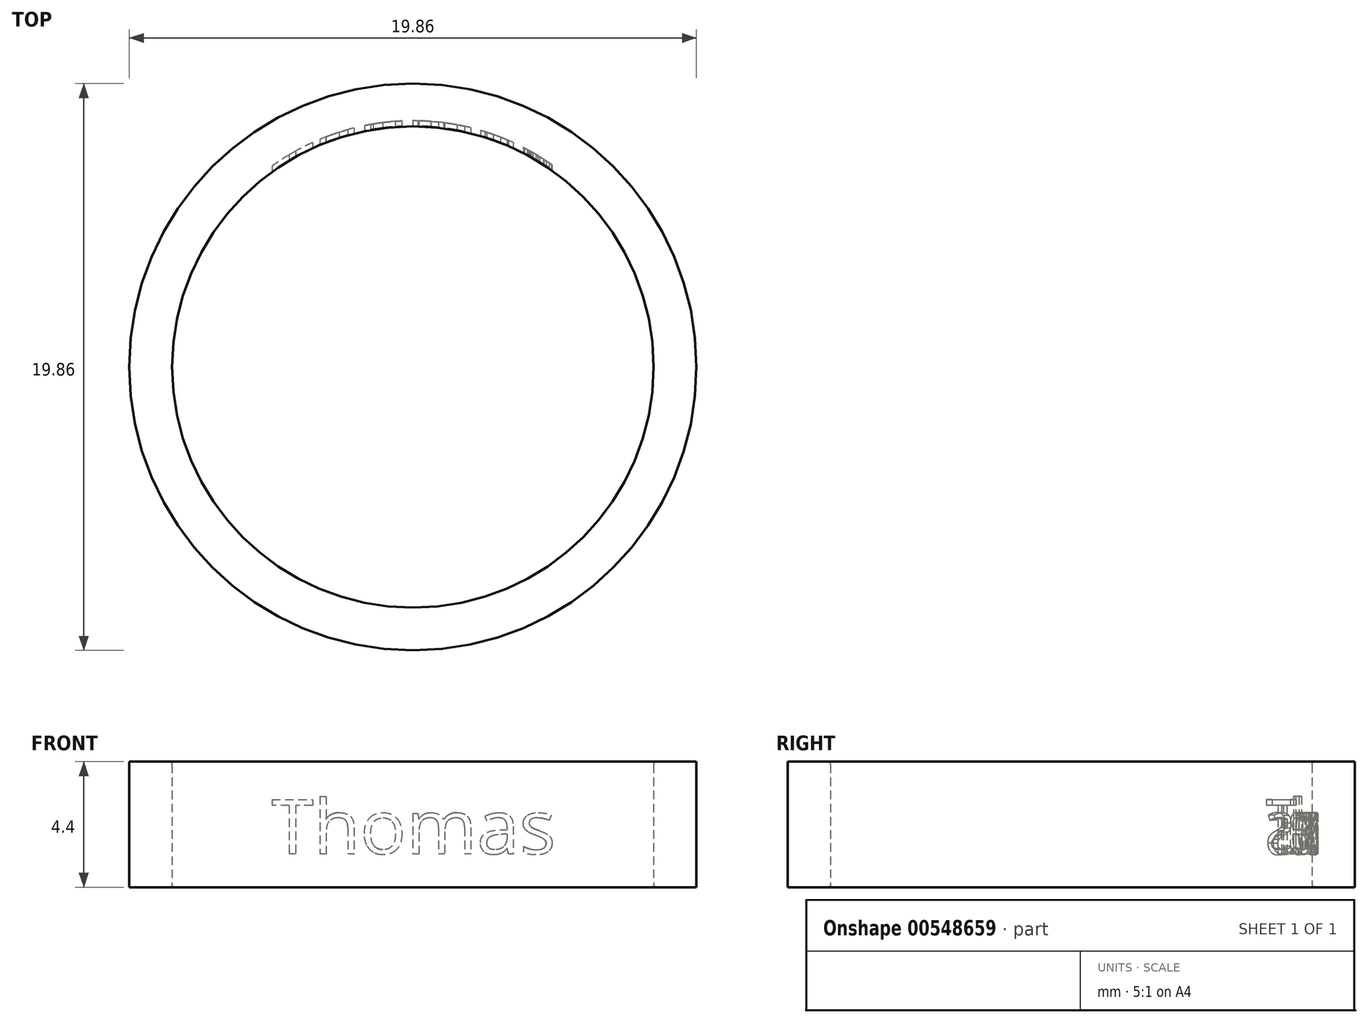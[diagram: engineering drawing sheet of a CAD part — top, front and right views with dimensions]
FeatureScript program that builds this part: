
annotation { "Feature Type Name" : "Feature", "Feature Type Description" : "" }
export const myFeature = defineFeature(function(context is Context, id is Id, definition is map)
    precondition{}
    {
        {
            var Q0;
            Q0=qCreatedBy(makeId("Top.planeOp"),FACE);
            var sketch = newSketch(context, id + "F0", { "sketchPlane" : qUnion([Q0])});
            skCircle(sketch, "E0", {"center": v(0, 0) * mm, "radius": 9.93 * mm});
            skCircle(sketch, "E1.0", {"center": v(0, 0) * mm, "radius": 8.43 * mm});
            skCircle(sketch, "E2.0", {"center": v(0, 0) * mm, "radius": 8.63 * mm, "construction": true});
            skSolve(sketch);
        }
        {
            var Q0;
            Q0=makeQuery(id+"F0.imprint","IMPRINT",FACE,{"disambiguationData":[TD([[makeQuery(id+"F0.imprint","IMPRINT",EDGE,{"derivedFrom":sQuery(id+"F0.wireOp",EDGE,"E0")}),1.0]])]});
            extrude(context, id + "F1", {"entities" : qUnion([Q0]), "depth" : 4.4 * mm, "offsetDistance" : 25 * mm});
        }
        {
            var Q0;
            Q0=qCreatedBy(makeId("Front.planeOp"),FACE);
            var sketch = newSketch(context, id + "F2", { "sketchPlane" : qUnion([Q0])});
            skText(sketch, "E3", { "text": "Thomas\n", "fontName": "OpenSans-Regular.ttf"});
            const initialGuessF2  = {"E3": [-0.00496, 0.00116, 1, 0, 0.00192]};
            skSetInitialGuess(sketch, initialGuessF2);
            skSolve(sketch);
        }
        {
            var Q0;
            Q0=qSketchRegion(id+"F2",true);
            var Q1;
            Q1=qConstructionFilter(qBodyType(qCreatedBy(id+"F2",EDGE),BodyType.WIRE),ConstructionObject.NO);
            var Q2;
            Q2=makeQuery(id+"F1.opExtrude","SWEPT_FACE",FACE,{"disambiguationData":[OSD([sQuery(id+"F0.wireOp",EDGE,"E1.0")])]});
            extrude(context, id + "F3", {"entities" : qUnion([Q0]), "operationType" : NewBodyOperationType.REMOVE, "surfaceEntities" : qUnion([Q1]), "endBound" : BoundingType.UP_TO_SURFACE, "oppositeDirection" : true, "depth" : 25 * mm, "endBoundEntityFace" : qUnion([Q2]), "hasOffset" : true, "offsetDistance" : 0.2 * mm, "offsetOppositeDirection" : true});
        }
        {
            var Q0;
            Q0=qSketchRegion(id+"F2",true);
            var Q1;
            Q1=makeQuery(id+"F1.opExtrude","SWEPT_FACE",FACE,{"disambiguationData":[OSD([sQuery(id+"F0.wireOp",EDGE,"E1.0")])]});
            extrude(context, id + "F4", {"entities" : qUnion([Q0]), "operationType" : NewBodyOperationType.REMOVE, "endBound" : BoundingType.UP_TO_SURFACE, "oppositeDirection" : true, "depth" : 25 * mm, "endBoundEntityFace" : qUnion([Q1]), "offsetDistance" : 25 * mm});
        }
        {
            var Q0;
            Q0=makeQuery(id+"F1.opExtrude","CAP_EDGE",EDGE,{"disambiguationData":[OSD([sQuery(id+"F0.wireOp",EDGE,"E1.0")])],"isStart":false});
            var Q1;
            Q1=makeQuery(id+"F1.opExtrude","CAP_EDGE",EDGE,{"disambiguationData":[OSD([sQuery(id+"F0.wireOp",EDGE,"E1.0")])],"isStart":true});
            fillet(context, id + "F5", {"entities" : qUnion([Q0, Q1]), "radius" : 0.1 * mm, "tangentPropagation" : true, "allowEdgeOverflow" : false});
        }
    });
